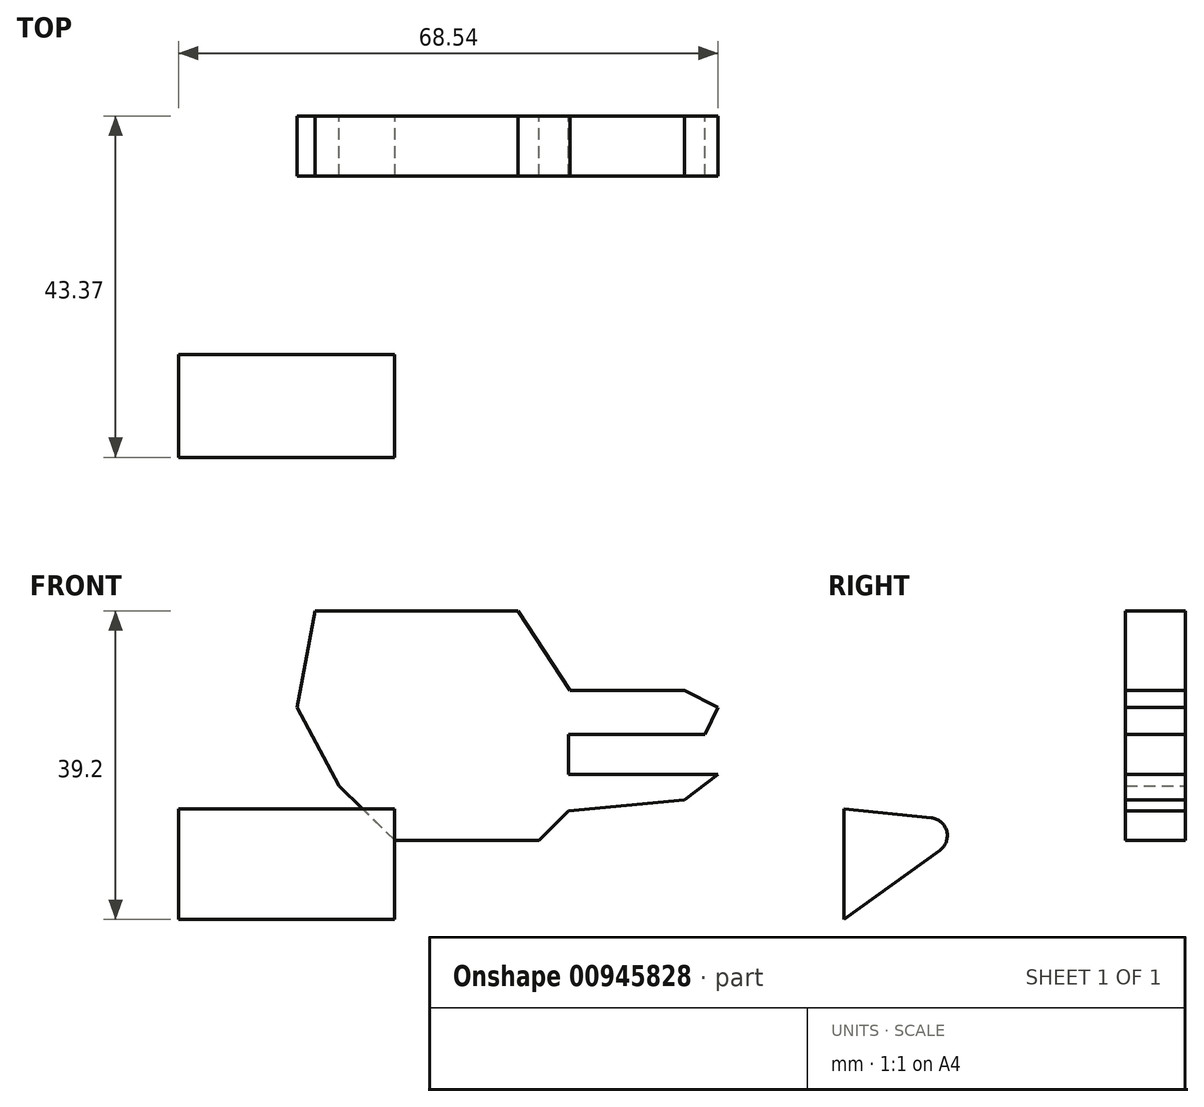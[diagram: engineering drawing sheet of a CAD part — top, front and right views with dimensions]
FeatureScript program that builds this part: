
annotation { "Feature Type Name" : "Feature", "Feature Type Description" : "" }
export const myFeature = defineFeature(function(context is Context, id is Id, definition is map)
    precondition{}
    {
        {
            var Q0;
            Q0=qCreatedBy(makeId("Front.planeOp"),FACE);
            var sketch = newSketch(context, id + "F0", { "sketchPlane" : qUnion([Q0])});
            skLineSegment(sketch, "E0", {"start": v(17.34, 39.2) * mm, "end": v(43.12, 39.2) * mm});
            skLineSegment(sketch, "E1", {"start": v(43.12, 39.2) * mm, "end": v(49.7, 29.07) * mm});
            skLineSegment(sketch, "E2", {"start": v(49.7, 29.07) * mm, "end": v(64.27, 29.07) * mm});
            skLineSegment(sketch, "E3", {"start": v(64.27, 29.07) * mm, "end": v(68.54, 26.94) * mm});
            skLineSegment(sketch, "E4", {"start": v(68.54, 26.94) * mm, "end": v(66.84, 23.52) * mm});
            skLineSegment(sketch, "E5", {"start": v(66.84, 23.52) * mm, "end": v(49.52, 23.52) * mm});
            skLineSegment(sketch, "E6", {"start": v(49.52, 23.52) * mm, "end": v(49.52, 18.4) * mm});
            skLineSegment(sketch, "E7", {"start": v(49.52, 18.4) * mm, "end": v(68.54, 18.4) * mm});
            skLineSegment(sketch, "E8", {"start": v(68.54, 18.4) * mm, "end": v(64.27, 15.2) * mm});
            skLineSegment(sketch, "E9", {"start": v(64.27, 15.2) * mm, "end": v(49.52, 13.78) * mm});
            skLineSegment(sketch, "E10", {"start": v(49.52, 13.78) * mm, "end": v(45.78, 10.05) * mm});
            skLineSegment(sketch, "E11", {"start": v(45.78, 10.05) * mm, "end": v(27.47, 10.05) * mm});
            skLineSegment(sketch, "E12", {"start": v(27.47, 10.05) * mm, "end": v(20.36, 16.98) * mm});
            skLineSegment(sketch, "E13", {"start": v(20.36, 16.98) * mm, "end": v(15.02, 26.94) * mm});
            skLineSegment(sketch, "E14", {"start": v(15.02, 26.94) * mm, "end": v(17.34, 39.2) * mm});
            skSolve(sketch);
        }
        {
            var Q0;
            Q0=makeQuery(id+"F0.imprint","IMPRINT",FACE,{"disambiguationData":[TD([[makeQuery(id+"F0.imprint","IMPRINT",EDGE,{"derivedFrom":sQuery(id+"F0.wireOp",EDGE,"E0")}),-1.0]])]});
            extrude(context, id + "F1", {"entities" : qUnion([Q0]), "depth" : 7.62 * mm, "offsetDistance" : 25.4 * mm});
        }
        {
            var Q0;
            Q0=qCreatedBy(makeId("Right.planeOp"),FACE);
            var sketch = newSketch(context, id + "F2", { "sketchPlane" : qUnion([Q0])});
            skLineSegment(sketch, "E15", {"start": v(-43.37, 14.05) * mm, "end": v(-43.37, 0) * mm});
            skLineSegment(sketch, "E16", {"start": v(-43.37, 0) * mm, "end": v(-26.37, 12.29) * mm});
            skLineSegment(sketch, "E17", {"start": v(-26.37, 12.29) * mm, "end": v(-43.37, 14.05) * mm});
            skSolve(sketch);
        }
        {
            var Q0;
            Q0=makeQuery(id+"F2.imprint","IMPRINT",FACE,{"disambiguationData":[TD([[makeQuery(id+"F2.imprint","IMPRINT",EDGE,{"derivedFrom":sQuery(id+"F2.wireOp",EDGE,"E15")}),1.0]])]});
            extrude(context, id + "F3", {"entities" : qUnion([Q0]), "depth" : 27.43 * mm, "offsetDistance" : 25.4 * mm});
        }
        {
            var Q0;
            Q0=makeQuery(id+"F3.opExtrude","SWEPT_EDGE",EDGE,{"disambiguationData":[OSD([sQuery(id+"F2.wireOp",EDGE,"E16"),sQuery(id+"F2.wireOp",EDGE,"E17")])]});
            fillet(context, id + "F4", {"entities" : qUnion([Q0]), "radius" : 2.28 * mm, "tangentPropagation" : true, "allowEdgeOverflow" : false});
        }
    });
